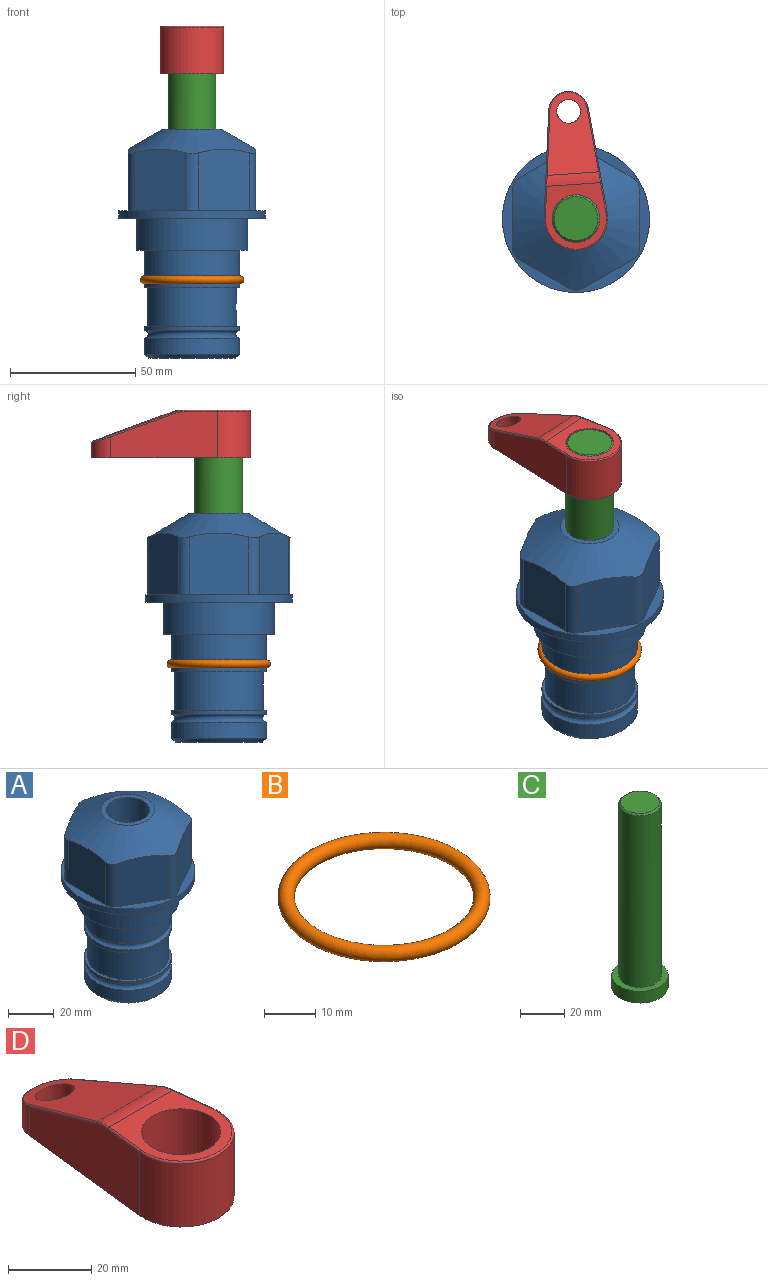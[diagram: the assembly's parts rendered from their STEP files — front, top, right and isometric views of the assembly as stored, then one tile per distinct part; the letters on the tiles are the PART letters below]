
ASSEMBLY  parts=4 mates=2
PART A: 36 faces, bbox 58.7x58.7x91.2 mm
  f0: cylinder r=17.78mm len=35.56mm, axis (0,0,1), area 1670.8mm2, adj f23,f24,f31
  f1: cylinder r=19.05mm len=38.1mm, axis (0,0,1), area 1191.9mm2, adj f26,f27,f30
  f2: plane 58.66x58.66mm, normal (0,0,-1), area 1150.6mm2, adj f3,f28
  f3: cylinder r=29.33mm len=58.66mm, axis (0,0,-1), area 585.1mm2, adj f2,f4
  f4: plane 58.66x58.66mm, normal (0,0,1), area 475.9mm2, adj f3,f5,f6,f7,f8,f9,f10,f11
  f5: plane 24.5x20.32mm, normal (-0.5,0.87,0), area 562.8mm2, adj f4,f15,f16,f17
  f6: plane 24.5x20.32mm, normal (0.5,0.87,0), area 562.8mm2, adj f4,f14,f15,f17
  f7: plane 24.5x23.48mm, normal (1,0,0), area 562.8mm2, adj f4,f13,f14,f17
  f8: plane 24.5x20.32mm, normal (0.5,-0.87,0), area 562.8mm2, adj f4,f12,f13,f17
  f9: plane 24.5x20.32mm, normal (-0.5,-0.87,0), area 562.8mm2, adj f4,f11,f12,f17
  f10: plane 24.5x23.48mm, normal (-1,0,0), area 562.8mm2, adj f4,f11,f16,f17
  f11: cylinder r=5.08mm len=23.01mm, axis (0,0,-1), area 121.2mm2, adj f4,f9,f10,f17
  f12: cylinder r=5.08mm len=23.01mm, axis (0,0,-1), area 121.2mm2, adj f4,f8,f9,f17
  f13: cylinder r=5.08mm len=23.01mm, axis (0,0,-1), area 121.2mm2, adj f4,f7,f8,f17
  f14: cylinder r=5.08mm len=23.01mm, axis (0,0,-1), area 121.2mm2, adj f4,f6,f7,f17
  f15: cylinder r=5.08mm len=23.01mm, axis (0,0,-1), area 121.2mm2, adj f4,f5,f6,f17
  f16: cylinder r=5.08mm len=23.01mm, axis (0,0,-1), area 121.2mm2, adj f4,f5,f10,f17
  f17: cone r=11.73mm half-angle=60deg, axis (0,0,-1), area 2071.8mm2, adj f5,f6,f7,f8,f9,f10,f11,f12
  f18: plane 23.46x23.46mm, normal (0,0,1), area 147.4mm2, adj f17,f35
  f19: plane 34.93x34.93mm, normal (0,0,-1), area 958mm2, adj f29
  f20: cylinder r=19.05mm len=38.1mm, axis (0,0,1), area 760.1mm2, adj f21,f29
  f21: torus R=19.05mm, axis (0,0,1), area 565.3mm2, adj f20,f22
  f22: cylinder r=19.05mm len=38.1mm, axis (0,0,1), area 190mm2, adj f21,f23
  f23: plane 38.1x38.1mm, normal (0,0,1), area 146.9mm2, adj f0,f22
  f24: plane 38.1x38.1mm, normal (0,0,-1), area 146.9mm2, adj f0,f25
  f25: cylinder r=19.05mm len=38.1mm, axis (0,0,1), area 190mm2, adj f24,f26
  f26: torus R=19.05mm, axis (0,0,1), area 565.3mm2, adj f1,f25
  f27: plane 44.45x44.45mm, normal (0,0,-1), area 411.7mm2, adj f1,f28
  f28: cylinder r=22.23mm len=44.45mm, axis (0,0,1), area 1773.5mm2, adj f2,f27
  f29: cone r=19.05mm half-angle=45deg, axis (0,0,1), area 257.5mm2, adj f19,f20
  f30: cylinder r=3.17mm len=6.75mm, axis (-1,0,0), area 128mm2, adj f1,f33
  f31: cylinder r=3.17mm len=6.35mm, axis (-1,0,0), area 102.5mm2, adj f0,f33
  f32: plane 25.4x25.4mm, normal (0,0,1), area 506.7mm2, adj f33
  f33: cylinder r=12.7mm len=66.42mm, axis (0,0,-1), area 5236.2mm2, adj f30,f31,f32,f34
  f34: cone r=9.53mm half-angle=30deg, axis (0,0,-1), area 443.4mm2, adj f33,f35
  f35: cylinder r=9.53mm len=19.05mm, axis (0,0,-1), area 849mm2, adj f18,f34
PART B: 1 faces, bbox 44.7x44.7x3.2 mm
  f0: torus R=19.05mm, axis (0,0,1), area 1193.9mm2
PART C: 6 faces, bbox 25.4x25.4x101.6 mm
  f0: plane 17.46x17.46mm, normal (0,0,1), area 239.5mm2, adj f5
  f1: plane 25.4x25.4mm, normal (0,0,-1), area 506.7mm2, adj f2
  f2: cylinder r=12.7mm len=25.4mm, axis (0,0,1), area 506.7mm2, adj f1,f3
  f3: plane 25.4x25.4mm, normal (0,0,1), area 221.7mm2, adj f2,f4
  f4: cylinder r=9.53mm len=94.46mm, axis (0,0,1), area 5653mm2, adj f3,f5
  f5: cone r=8.73mm half-angle=45deg, axis (0,0,-1), area 64.4mm2, adj f0,f4
PART D: 44 faces, bbox 27.5x64.5x19.1 mm
  f0: plane 2.3x0.95mm, normal (0,0,-1), area 1mm2, adj f25,f30,f34
  f1: plane 63.5x25.4mm, normal (0,0,-1), area 561.7mm2, adj f2,f3,f4,f5,f6,f7,f19,f20
  f2: cylinder r=12.7mm len=25.4mm, axis (0,0,-1), area 792.2mm2, adj f1,f3,f5,f13
  f3: plane 42.33x18.54mm, normal (0.99,0.11,0), area 647mm2, adj f1,f2,f4,f11,f12,f14
  f4: cylinder r=7.94mm len=15.78mm, axis (0,0,-1), area 158.6mm2, adj f1,f3,f5,f16
  f5: plane 42.33x18.54mm, normal (-0.99,0.11,0), area 647mm2, adj f1,f2,f4,f15,f17,f18
  f6: cylinder r=9.53mm len=19.05mm, axis (0,0,-1), area 1140.1mm2, adj f1,f8
  f7: cylinder r=4.76mm len=10.98mm, axis (0,0,-1), area 276.1mm2, adj f1,f9
  f8: plane 25.83x24.38mm, normal (0,0,1), area 262.2mm2, adj f6,f10,f11,f13,f15
  f9: plane 32.49x20.55mm, normal (0,0.34,0.94), area 489.9mm2, adj f7,f10,f14,f16,f18
  f10: cylinder r=12.7mm len=21.49mm, axis (-1,0,0), area 93.2mm2, adj f8,f9,f12,f17
  f11: cylinder r=0.51mm len=12.34mm, axis (0.11,-0.99,0), area 9.9mm2, adj f3,f8,f12,f13
  f12: bspline ~7.62x1.64mm, area 3.5mm2, adj f3,f10,f11,f14
  f13: torus R=12.19mm, axis (0,0,1), area 33.6mm2, adj f2,f8,f11,f15
  f14: cylinder r=0.51mm len=26.01mm, axis (0.1,-0.93,0.34), area 21.6mm2, adj f3,f9,f12,f16
  f15: cylinder r=0.51mm len=12.34mm, axis (0.11,0.99,0), area 9.9mm2, adj f5,f8,f13,f17
  f16: bspline ~15.78x7.05mm, area 15.7mm2, adj f4,f9,f14,f18
  f17: bspline ~7.62x1.64mm, area 3.5mm2, adj f5,f10,f15,f18
  f18: cylinder r=0.51mm len=26.01mm, axis (0.1,0.93,-0.34), area 21.6mm2, adj f5,f9,f16,f17
  f19: plane 21.6x14.29mm, normal (-0.99,-0.11,0), area 242.6mm2, adj f1,f26,f28,f34,f36,f38
  f20: plane 21.6x14.29mm, normal (0.99,-0.11,0), area 242.6mm2, adj f1,f27,f29,f37,f39,f41
  f21: cylinder r=12.7mm len=14.29mm, axis (0,0,-1), area 173.2mm2, adj f1,f26,f27,f30,f31,f33
  f22: cylinder r=7.94mm len=7.63mm, axis (0,0,-1), area 53.8mm2, adj f1,f28,f29,f42
  f23: plane 2.3x0.95mm, normal (0,0,-1), area 1mm2, adj f25,f33,f37
  f24: plane 17.94x12.32mm, normal (0,-0.34,-0.94), area 191.2mm2, adj f25,f38,f41,f42
  f25: cylinder r=9.53mm len=12.93mm, axis (-1,0,0), area 37.5mm2, adj f0,f23,f24,f31,f36,f39
  f26: cylinder r=1.59mm len=14.29mm, axis (0,0,-1), area 49mm2, adj f1,f19,f21,f32
  f27: cylinder r=1.59mm len=14.29mm, axis (0,0,-1), area 49mm2, adj f1,f20,f21,f35
  f28: cylinder r=1.59mm len=7.28mm, axis (0,0,-1), area 22.1mm2, adj f1,f19,f22,f40
  f29: cylinder r=1.59mm len=7.28mm, axis (0,0,-1), area 22.1mm2, adj f1,f20,f22,f43
  f30: torus R=14.29mm, axis (0,0,1), area 5.8mm2, adj f0,f21,f31,f32
  f31: bspline ~11.06x2.73mm, area 20.8mm2, adj f21,f25,f30,f33
  f32: sphere r=1.59mm, area 5.4mm2, adj f26,f30,f34
  f33: torus R=14.29mm, axis (0,0,1), area 5.8mm2, adj f21,f23,f31,f35
  f34: cylinder r=1.59mm len=1.68mm, axis (-0.11,0.99,0), area 2.4mm2, adj f0,f19,f32,f36
  f35: sphere r=1.59mm, area 5.4mm2, adj f27,f33,f37
  f36: bspline ~5.82x2.33mm, area 7.7mm2, adj f19,f25,f34,f38
  f37: cylinder r=1.59mm len=1.68mm, axis (0.11,0.99,0), area 2.4mm2, adj f20,f23,f35,f39
  f38: cylinder r=1.59mm len=18.33mm, axis (0.1,-0.93,0.34), area 46.7mm2, adj f19,f24,f36,f40
  f39: bspline ~5.82x2.33mm, area 7.7mm2, adj f20,f25,f37,f41
  f40: sphere r=1.59mm, area 3.6mm2, adj f28,f38,f42
  f41: cylinder r=1.59mm len=18.33mm, axis (0.1,0.93,-0.34), area 46.7mm2, adj f20,f24,f39,f43
  f42: bspline ~8.31x1.84mm, area 15.3mm2, adj f22,f24,f40,f43
  f43: sphere r=1.59mm, area 3.6mm2, adj f29,f41,f42
PLACE A at identity fixed
PLACE B at identity
PLACE C rot(axis=(0,0,1),3.9deg) t=(0,0,3.09)mm
PLACE D rot(axis=(0,0,1),3.9deg) t=(0,0,57.7)mm
MATE cylindrical C.f2 <-> A.f0  axis (0,0,1) through (0,0,28.73)mm
MATE fastened D.f2 <-> C.f2  axis (0,0,-1) through (0,0,76.75)mm
